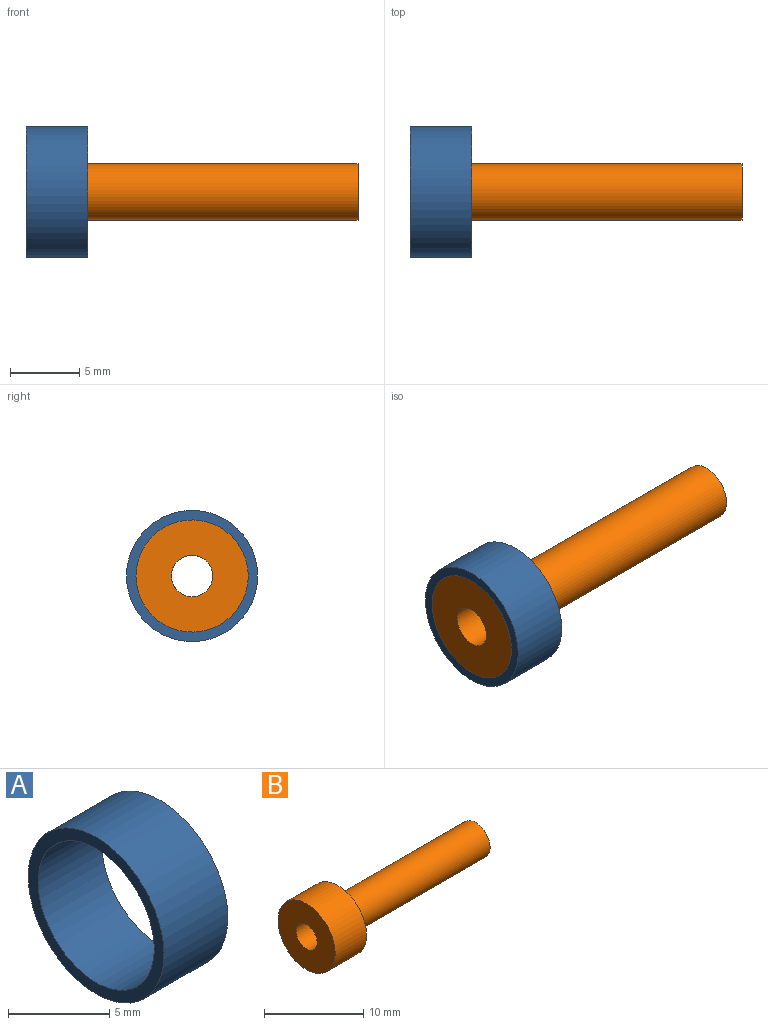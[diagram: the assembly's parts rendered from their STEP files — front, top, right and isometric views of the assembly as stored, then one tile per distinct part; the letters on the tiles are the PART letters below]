
ASSEMBLY  parts=2 mates=1
PART A: 4 faces, bbox 4.5x9.5x9.5 mm
  f0: cylinder r=4.06mm len=8.13mm, axis (-1,0,0), area 114.2mm2, adj f2,f3
  f1: cylinder r=4.75mm len=9.5mm, axis (-1,0,0), area 133.4mm2, adj f2,f3
  f2: plane 9.5x9.5mm, normal (1,0,0), area 19mm2, adj f0,f1
  f3: plane 9.5x9.5mm, normal (-1,0,0), area 19mm2, adj f0,f1
PART B: 6 faces, bbox 24.1x8.1x8.1 mm
  f0: cylinder r=4.06mm len=8.13mm, axis (-1,0,0), area 114.2mm2, adj f1,f2
  f1: plane 8.13x8.13mm, normal (1,0,0), area 38.6mm2, adj f0,f3
  f2: plane 8.13x8.13mm, normal (-1,0,0), area 44.8mm2, adj f0,f5
  f3: cylinder r=2.06mm len=19.58mm, axis (-1,0,0), area 253.2mm2, adj f1,f4
  f4: plane 4.11x4.11mm, normal (1,0,0), area 6.2mm2, adj f3,f5
  f5: cylinder r=1.5mm len=24.05mm, axis (1,0,0), area 226.7mm2, adj f2,f4
PLACE A t=(12.48,57.08,-1.3)mm
PLACE B t=(12.48,29.33,-0.22)mm
MATE fastened A.f0 <-> B.f0  axis (1,0,0) through (16.95,42.73,1.03)mm
